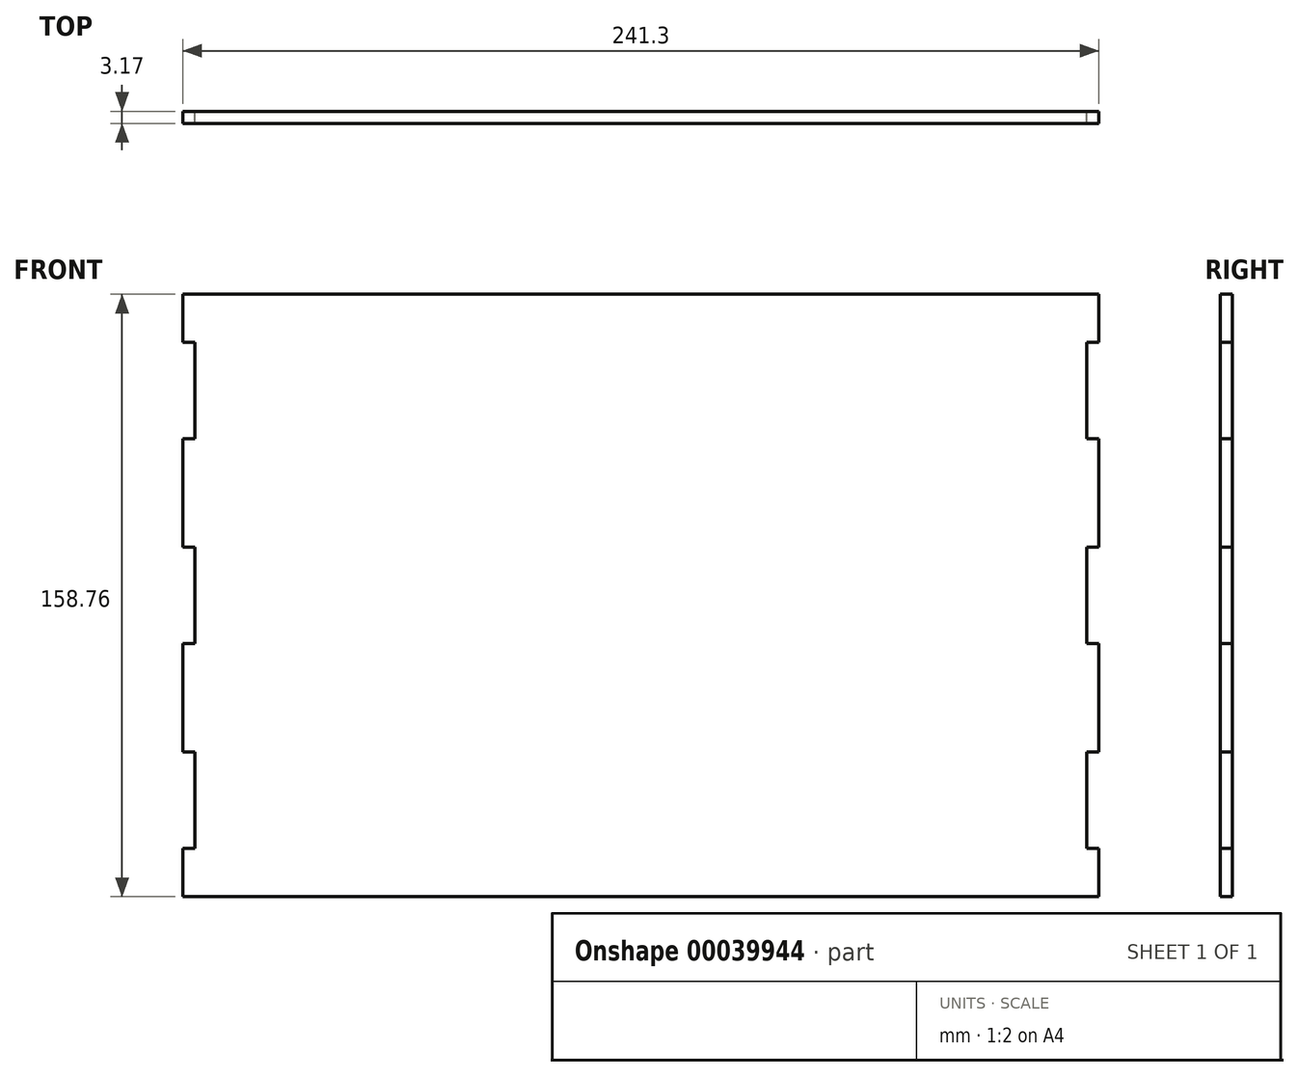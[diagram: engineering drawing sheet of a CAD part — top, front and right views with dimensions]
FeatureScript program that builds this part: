
annotation { "Feature Type Name" : "Feature", "Feature Type Description" : "" }
export const myFeature = defineFeature(function(context is Context, id is Id, definition is map)
    precondition{}
    {
        {
            var Q0;
            Q0=qCreatedBy(makeId("Front.planeOp"),FACE);
            var sketch = newSketch(context, id + "F0", { "sketchPlane" : qUnion([Q0])});
            skLineSegment(sketch, "E0.rect.bottom", {"start": v(120.65, -79.38) * mm, "end": v(-120.65, -79.38) * mm});
            skLineSegment(sketch, "E0.rect.top", {"start": v(120.65, 79.38) * mm, "end": v(-120.65, 79.38) * mm});
            skLineSegment(sketch, "E0.rect.left", {"start": v(120.65, -79.38) * mm, "end": v(120.65, 79.38) * mm});
            skLineSegment(sketch, "E0.rect.right", {"start": v(-120.65, -79.38) * mm, "end": v(-120.65, 79.38) * mm});
            skPoint(sketch, "E0.rect.middle", {"position": v(0, 0) * mm});
            skLineSegment(sketch, "E1", {"start": v(-120.65, 66.68) * mm, "end": v(-117.47, 66.68) * mm});
            skLineSegment(sketch, "E2", {"start": v(-117.48, 66.68) * mm, "end": v(-117.48, 41.28) * mm});
            skLineSegment(sketch, "E3", {"start": v(-117.47, 41.28) * mm, "end": v(-120.65, 41.28) * mm});
            skLineSegment(sketch, "E4", {"start": v(-120.65, -66.68) * mm, "end": v(-117.48, -66.68) * mm});
            skLineSegment(sketch, "E5", {"start": v(-117.48, -66.68) * mm, "end": v(-117.48, -41.28) * mm});
            skLineSegment(sketch, "E6", {"start": v(-117.48, -41.28) * mm, "end": v(-120.65, -41.28) * mm});
            skLineSegment(sketch, "E7", {"start": v(-117.48, 41.28) * mm, "end": v(-117.48, -41.28) * mm, "construction": true});
            skLineSegment(sketch, "E8", {"start": v(-117.48, 0) * mm, "end": v(-117.48, -12.7) * mm});
            skLineSegment(sketch, "E9", {"start": v(-117.48, -12.7) * mm, "end": v(-120.65, -12.7) * mm});
            skLineSegment(sketch, "E10", {"start": v(-117.48, 0) * mm, "end": v(-117.48, 12.7) * mm});
            skLineSegment(sketch, "E11", {"start": v(-117.48, 12.7) * mm, "end": v(-120.65, 12.7) * mm});
            skLineSegment(sketch, "E12", {"start": v(0, 79.38) * mm, "end": v(0, -79.38) * mm, "construction": true});
            skLineSegment(sketch, "E13.MirrorCS", {"start": v(117.47, 66.68) * mm, "end": v(117.47, 41.28) * mm});
            skLineSegment(sketch, "E14.MirrorCS", {"start": v(120.65, 66.68) * mm, "end": v(117.47, 66.68) * mm});
            skLineSegment(sketch, "E15.MirrorCS", {"start": v(117.47, 41.28) * mm, "end": v(120.65, 41.28) * mm});
            skLineSegment(sketch, "E16.MirrorCS", {"start": v(117.48, 12.7) * mm, "end": v(120.65, 12.7) * mm});
            skLineSegment(sketch, "E17.MirrorCS", {"start": v(117.48, 0) * mm, "end": v(117.48, 12.7) * mm});
            skLineSegment(sketch, "E18.MirrorCS", {"start": v(117.48, 0) * mm, "end": v(117.48, -12.7) * mm});
            skLineSegment(sketch, "E19.MirrorCS", {"start": v(117.48, -12.7) * mm, "end": v(120.65, -12.7) * mm});
            skLineSegment(sketch, "E20.MirrorCS", {"start": v(117.48, -41.27) * mm, "end": v(120.65, -41.27) * mm});
            skLineSegment(sketch, "E21.MirrorCS", {"start": v(120.65, -66.67) * mm, "end": v(117.48, -66.67) * mm});
            skLineSegment(sketch, "E22.MirrorCS", {"start": v(117.48, -66.67) * mm, "end": v(117.48, -41.27) * mm});
            skSolve(sketch);
        }
        {
            var Q0;
            Q0=makeQuery(id+"F0.imprint","IMPRINT",FACE,{"disambiguationData":[TD([[makeQuery(id+"F0.imprint","IMPRINT",EDGE,{"derivedFrom":sQuery(id+"F0.wireOp",EDGE,"E0.rect.bottom")}),-1.0]])]});
            extrude(context, id + "F1", {"entities" : qUnion([Q0]), "depth" : 3.17 * mm});
        }
    });
